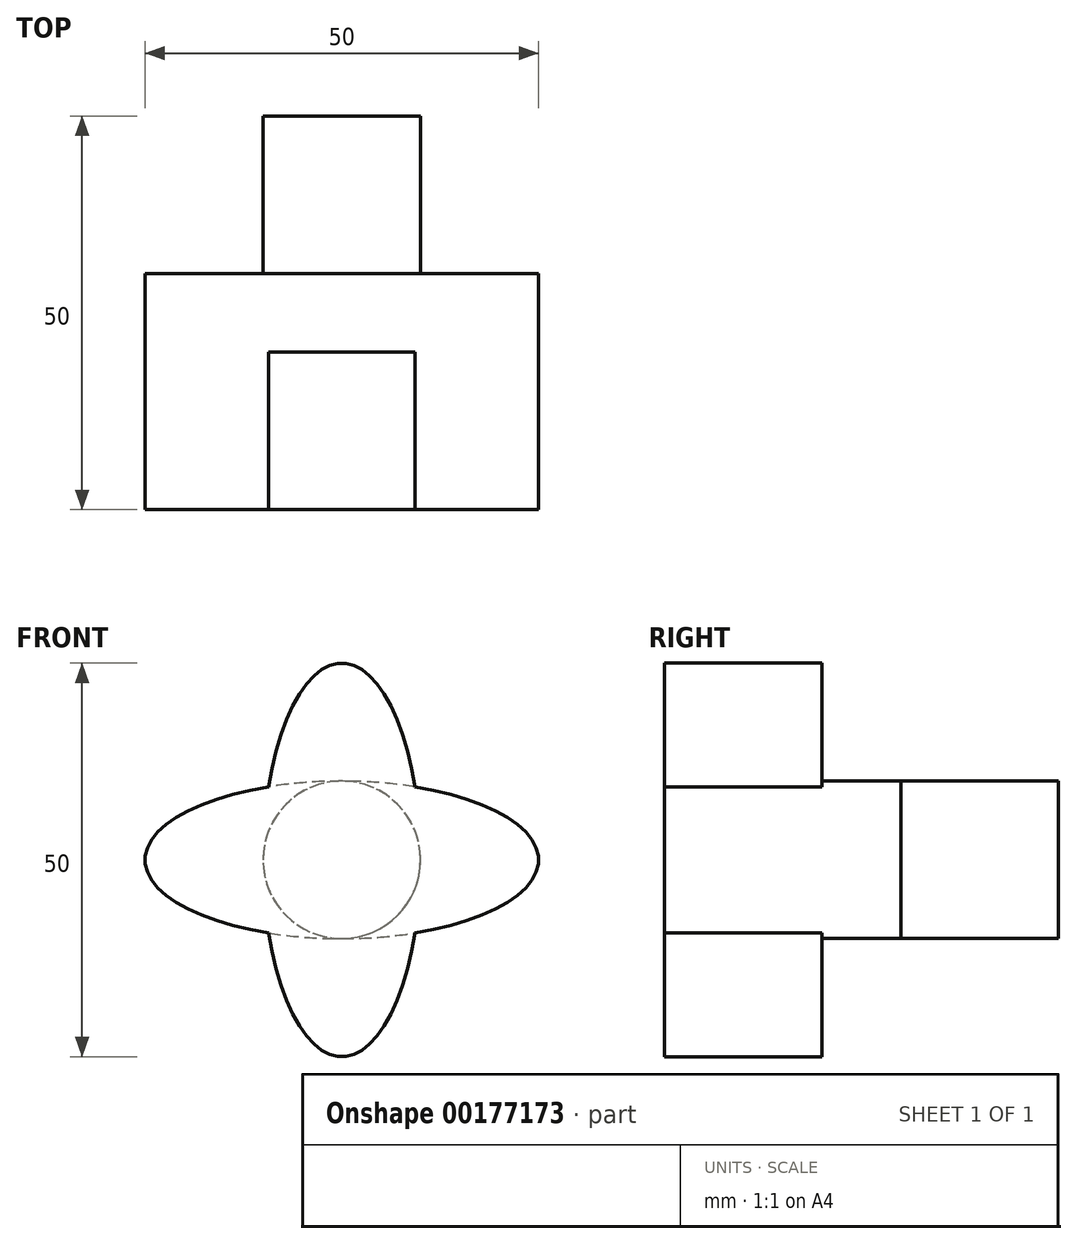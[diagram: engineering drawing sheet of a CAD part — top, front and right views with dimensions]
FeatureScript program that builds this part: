
annotation { "Feature Type Name" : "Feature", "Feature Type Description" : "" }
export const myFeature = defineFeature(function(context is Context, id is Id, definition is map)
    precondition{}
    {
        {
            var Q0;
            Q0=qCreatedBy(makeId("Front.planeOp"),FACE);
            var sketch = newSketch(context, id + "F0", { "sketchPlane" : qUnion([Q0])});
            skEllipse(sketch, "E0", {"center": v(0, 0) * mm, "majorRadius": 25 * mm, "minorRadius": 10 * mm, "majorAxis": v(-1, 0)});
            skSolve(sketch);
        }
        {
            var Q0;
            Q0 = qSketchRegion(id + "F0", true);
            extrude(context, id + "F1", {"entities" : qUnion([Q0]), "depth" : 10 * mm});
        }
        {
            var Q0;
            Q0=qCreatedBy(makeId("Front.planeOp"),FACE);
            var sketch = newSketch(context, id + "F2", { "sketchPlane" : qUnion([Q0])});
            skCircle(sketch, "E1", {"center": v(0, 0) * mm, "radius": 10 * mm});
            skSolve(sketch);
        }
        {
            var Q0;
            Q0 = qSketchRegion(id + "F2", true);
            extrude(context, id + "F3", {"entities" : qUnion([Q0]), "operationType" : NewBodyOperationType.ADD, "oppositeDirection" : true, "depth" : 20 * mm});
        }
        {
            var Q0;
            Q0=makeQuery(id+"F1.opExtrude","CAP_FACE",FACE,{"disambiguationData":[OSD([sQuery(id+"F0.wireOp",EDGE,"KEWCKqeL-DSg9-luIp-IGd3-z7bYKLh19cfc"),sQuery(id+"F0.wireOp",EDGE,"E0")])],"isStart":false});
            var sketch = newSketch(context, id + "F4", { "sketchPlane" : qUnion([Q0])});
            skEllipse(sketch, "E2", {"center": v(0, 0) * mm, "majorRadius": 25 * mm, "minorRadius": 10 * mm, "majorAxis": v(1, 0)});
            skEllipse(sketch, "E3", {"center": v(0, 0) * mm, "majorRadius": 25 * mm, "minorRadius": 10 * mm, "majorAxis": v(0, 1)});
            skSolve(sketch);
        }
        {
            var Q0;
            Q0 = qSketchRegion(id + "F4", true);
            extrude(context, id + "F5", {"entities" : qUnion([Q0]), "operationType" : NewBodyOperationType.ADD, "depth" : 20 * mm});
        }
    });
